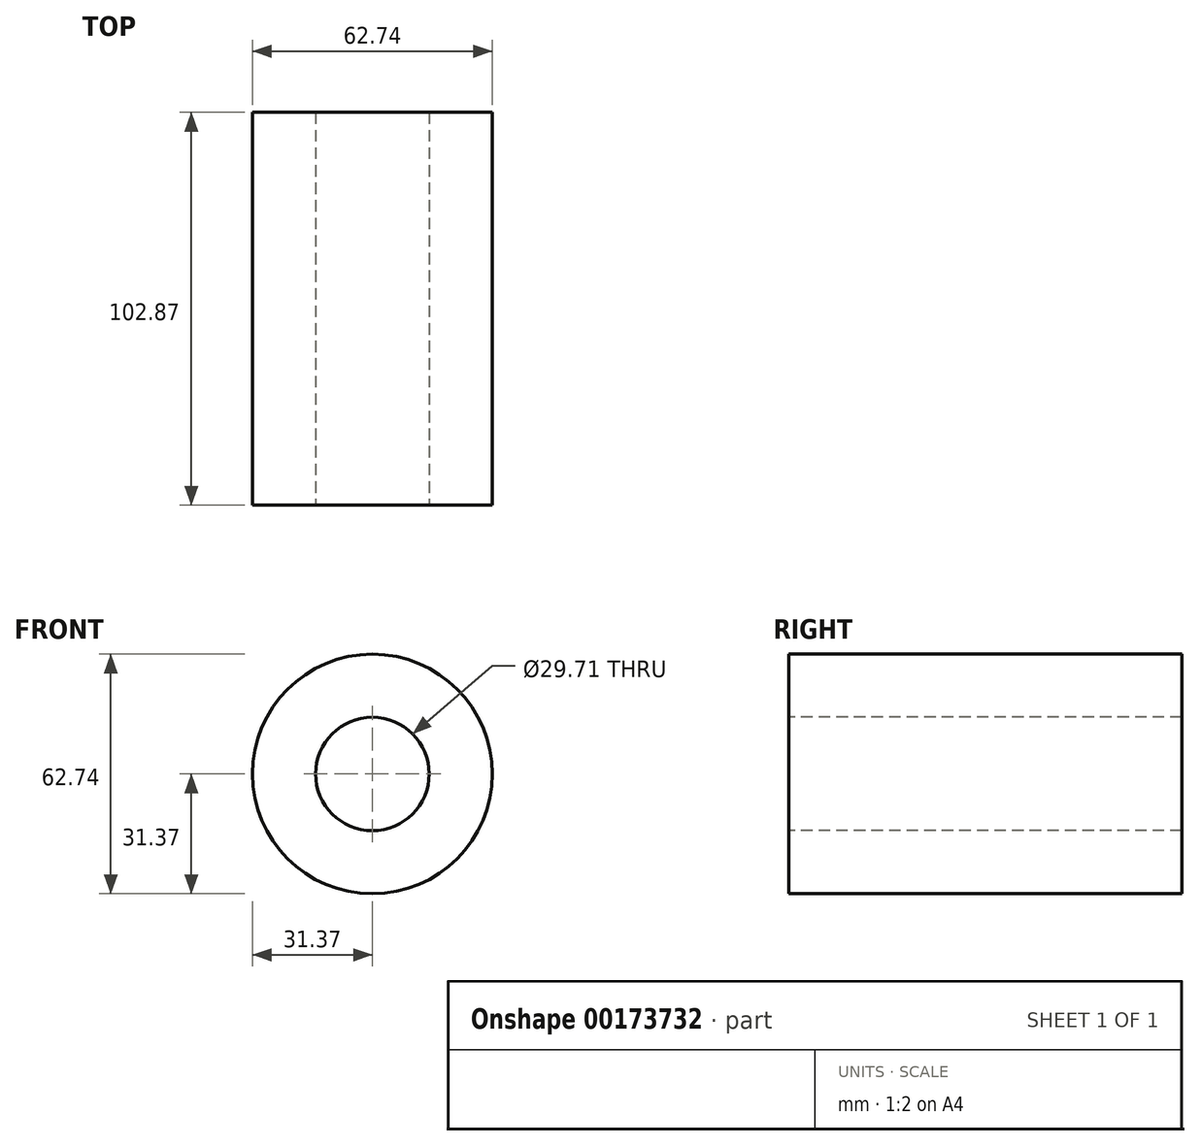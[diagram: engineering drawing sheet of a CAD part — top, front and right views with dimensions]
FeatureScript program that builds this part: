
annotation { "Feature Type Name" : "Feature", "Feature Type Description" : "" }
export const myFeature = defineFeature(function(context is Context, id is Id, definition is map)
    precondition{}
    {
        {
            var Q0;
            Q0=qCreatedBy(makeId("Front.planeOp"),FACE);
            var sketch = newSketch(context, id + "F0", { "sketchPlane" : qUnion([Q0])});
            skCircle(sketch, "E0", {"center": v(0, 0) * mm, "radius": 31.37 * mm});
            skSolve(sketch);
        }
        {
            var Q0;
            Q0=makeQuery(id+"F0.imprint","IMPRINT",FACE,{"disambiguationData":[TD([[makeQuery(id+"F0.imprint","IMPRINT",EDGE,{"derivedFrom":sQuery(id+"F0.wireOp",EDGE,"E0")}),1.0]])]});
            extrude(context, id + "F1", {"entities" : qUnion([Q0]), "oppositeDirection" : true, "depth" : 102.87 * mm});
        }
        {
            var Q0;
            Q0=makeQuery(id+"F1.opExtrude","CAP_FACE",FACE,{"disambiguationData":[OSD([sQuery(id+"F0.wireOp",EDGE,"E0")])],"isStart":true});
            var sketch = newSketch(context, id + "F2", { "sketchPlane" : qUnion([Q0])});
            skCircle(sketch, "E1", {"center": v(0, 0) * mm, "radius": 14.85 * mm});
            skSolve(sketch);
        }
        {
            var Q0;
            Q0=makeQuery(id+"F2.imprint","IMPRINT",FACE,{"disambiguationData":[TD([[makeQuery(id+"F2.imprint","IMPRINT",EDGE,{"derivedFrom":sQuery(id+"F2.wireOp",EDGE,"E1")}),1.0]])]});
            extrude(context, id + "F3", {"entities" : qUnion([Q0]), "operationType" : NewBodyOperationType.REMOVE, "endBound" : BoundingType.SYMMETRIC, "oppositeDirection" : true, "depth" : 508 * mm});
        }
    });
